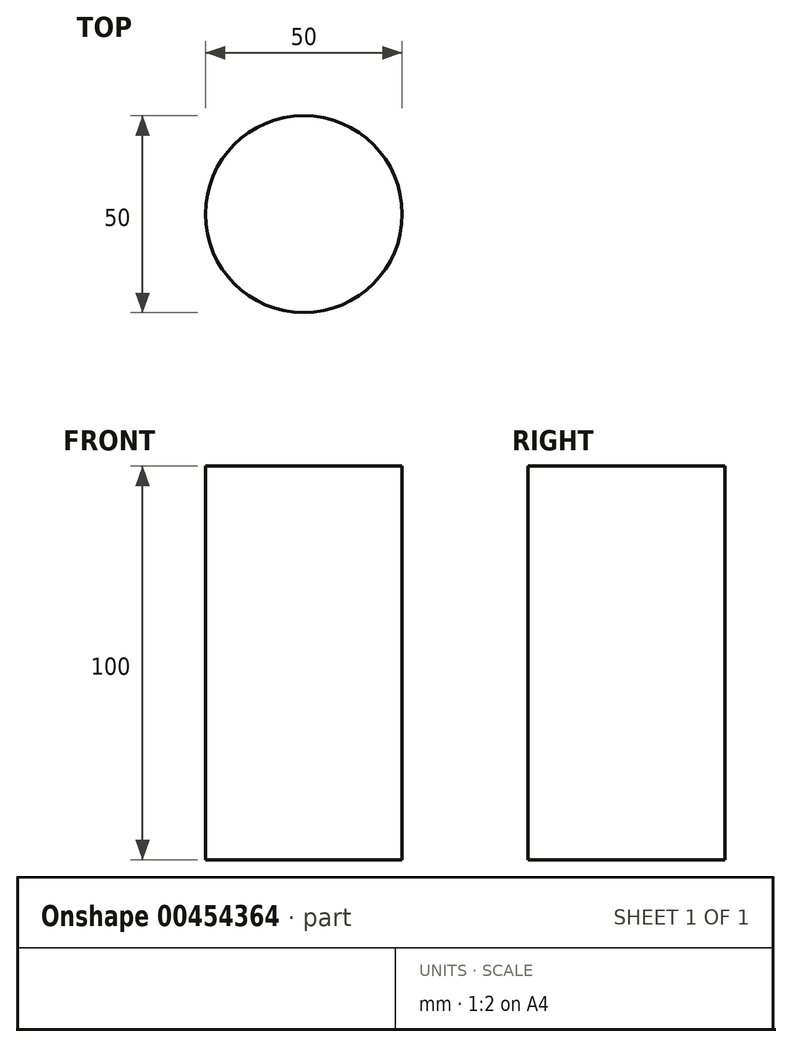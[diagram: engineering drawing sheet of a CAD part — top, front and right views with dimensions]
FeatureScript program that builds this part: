
annotation { "Feature Type Name" : "Feature", "Feature Type Description" : "" }
export const myFeature = defineFeature(function(context is Context, id is Id, definition is map)
    precondition{}
    {
        {
            var Q0;
            Q0=qCreatedBy(makeId("Top.planeOp"),FACE);
            var sketch = newSketch(context, id + "F0", { "sketchPlane" : qUnion([Q0])});
            skCircle(sketch, "E0", {"center": v(0, 0) * mm, "radius": 25 * mm});
            skSolve(sketch);
        }
        {
            var Q0;
            Q0=qSketchRegion(id+"F0",true);
            extrude(context, id + "F1", {"entities" : qUnion([Q0]), "depth" : 100 * mm});
        }
    });
